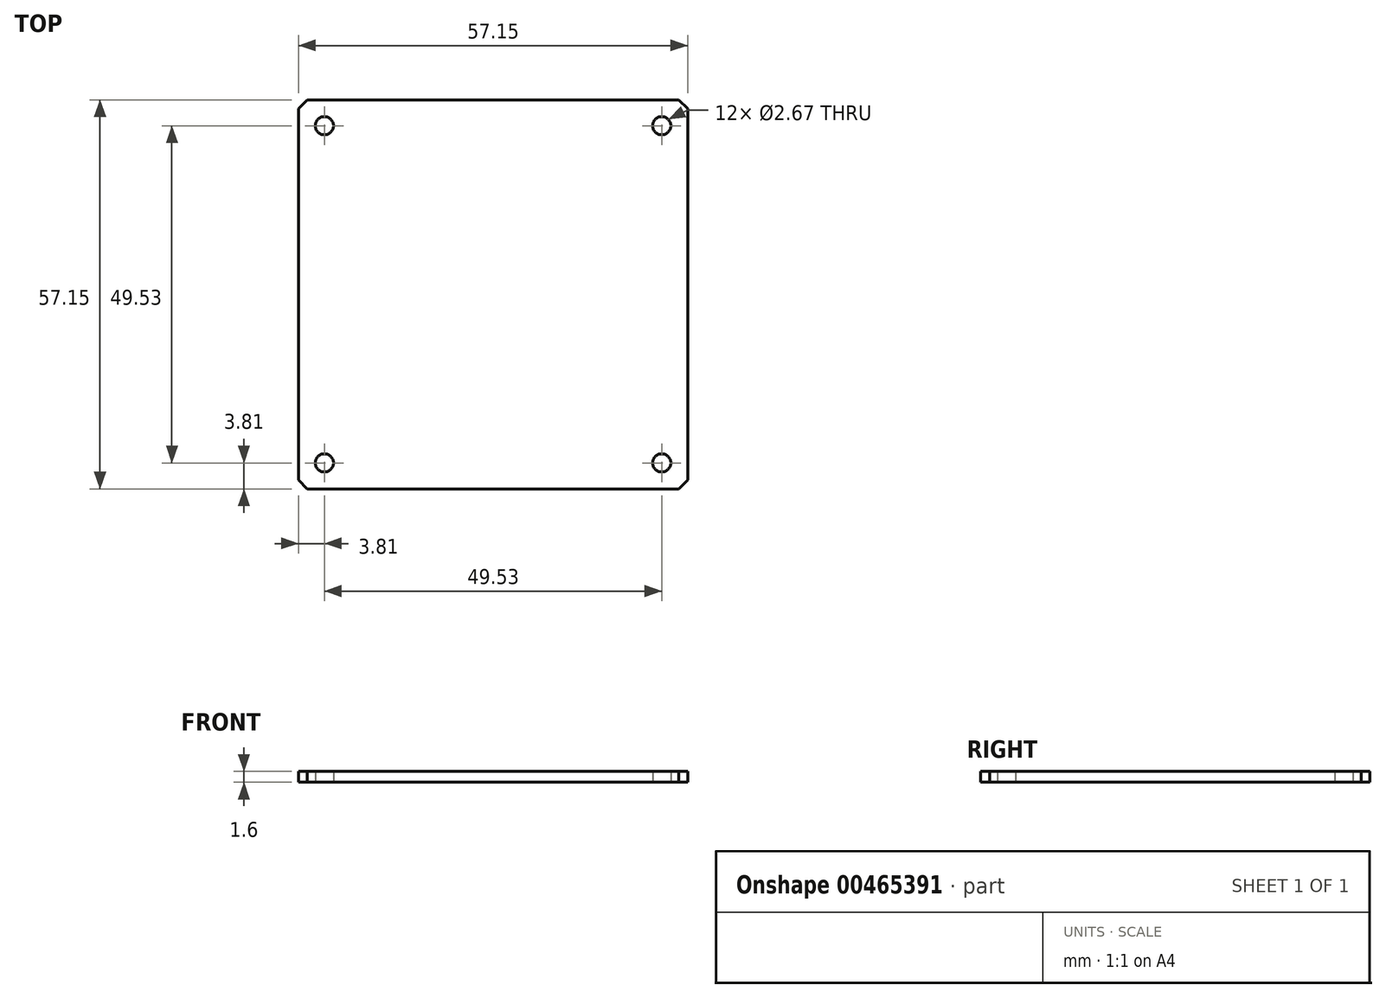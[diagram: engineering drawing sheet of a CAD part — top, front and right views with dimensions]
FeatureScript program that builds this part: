
annotation { "Feature Type Name" : "Feature", "Feature Type Description" : "" }
export const myFeature = defineFeature(function(context is Context, id is Id, definition is map)
    precondition{}
    {
        {
            var Q0;
            Q0=qCreatedBy(makeId("Top.planeOp"),FACE);
            var sketch = newSketch(context, id + "F0", { "sketchPlane" : qUnion([Q0])});
            skLineSegment(sketch, "E0.bottom", {"start": v(0, 0) * mm, "end": v(57.15, 0) * mm});
            skLineSegment(sketch, "E0.top", {"start": v(0, -57.15) * mm, "end": v(57.15, -57.15) * mm});
            skLineSegment(sketch, "E0.left", {"start": v(0, 0) * mm, "end": v(0, -57.15) * mm});
            skLineSegment(sketch, "E0.right", {"start": v(57.15, 0) * mm, "end": v(57.15, -57.15) * mm});
            skCircle(sketch, "E1", {"center": v(53.34, -3.8) * mm, "radius": 1.33 * mm});
            skLineSegment(sketch, "E2", {"start": v(57.15, -28.58) * mm, "end": v(0, -28.58) * mm, "construction": true});
            skLineSegment(sketch, "E3", {"start": v(28.58, 0) * mm, "end": v(28.58, -57.15) * mm, "construction": true});
            skLineSegment(sketch, "E4", {"start": v(55.87, 0) * mm, "end": v(57.15, -1.28) * mm});
            skCircle(sketch, "E5.MirrorC", {"center": v(53.34, -53.34) * mm, "radius": 1.33 * mm});
            skLineSegment(sketch, "E6.MirrorCS", {"start": v(55.87, -57.15) * mm, "end": v(57.15, -55.87) * mm});
            skCircle(sketch, "E7.MirrorC", {"center": v(3.81, -53.34) * mm, "radius": 1.33 * mm});
            skCircle(sketch, "E8.MirrorC", {"center": v(3.81, -3.8) * mm, "radius": 1.33 * mm});
            skLineSegment(sketch, "E9.MirrorCS", {"start": v(1.28, -57.15) * mm, "end": v(0, -55.87) * mm});
            skLineSegment(sketch, "E10.MirrorCS", {"start": v(1.28, 0) * mm, "end": v(0, -1.28) * mm});
            skSolve(sketch);
        }
        {
            var Q0;
            Q0=makeQuery(id+"F0.imprint","IMPRINT",FACE,{"disambiguationData":[TD([[makeQuery(id+"F0.imprint","IMPRINT",EDGE,{"derivedFrom":sQuery(id+"F0.wireOp",EDGE,"E1")}),-1.0]])]});
            extrude(context, id + "F1", {"entities" : qUnion([Q0]), "depth" : 1.6 * mm, "offsetDistance" : 25 * mm});
        }
        {
            var Q0;
            Q0=makeQuery(id+"F1.opExtrude","CAP_FACE",FACE,{"disambiguationData":[OSD([sQuery(id+"F0.wireOp",EDGE,"E0.bottom"),sQuery(id+"F0.wireOp",EDGE,"E0.top"),sQuery(id+"F0.wireOp",EDGE,"E0.left"),sQuery(id+"F0.wireOp",EDGE,"E0.right"),sQuery(id+"F0.wireOp",EDGE,"E1"),sQuery(id+"F0.wireOp",EDGE,"E4"),sQuery(id+"F0.wireOp",EDGE,"E5.MirrorC"),sQuery(id+"F0.wireOp",EDGE,"E6.MirrorCS"),sQuery(id+"F0.wireOp",EDGE,"E7.MirrorC"),sQuery(id+"F0.wireOp",EDGE,"E8.MirrorC"),sQuery(id+"F0.wireOp",EDGE,"E9.MirrorCS"),sQuery(id+"F0.wireOp",EDGE,"E10.MirrorCS")])],"isStart":false});
            var sketch = newSketch(context, id + "F2", { "sketchPlane" : qUnion([Q0])});
            skLineSegment(sketch, "E11", {"start": v(28.58, -57.15) * mm, "end": v(28.58, 0) * mm, "construction": true});
            skPoint(sketch, "E12", {"position": v(28.58, -50.8) * mm});
            skPoint(sketch, "E13", {"position": v(28.58, -6.35) * mm});
            skSolve(sketch);
        }
        {
            var Q0;
            Q0=makeQuery(id+"F1.opExtrude","CAP_FACE",FACE,{"disambiguationData":[OSD([sQuery(id+"F0.wireOp",EDGE,"E0.bottom"),sQuery(id+"F0.wireOp",EDGE,"E0.top"),sQuery(id+"F0.wireOp",EDGE,"E0.left"),sQuery(id+"F0.wireOp",EDGE,"E0.right"),sQuery(id+"F0.wireOp",EDGE,"E1"),sQuery(id+"F0.wireOp",EDGE,"E4"),sQuery(id+"F0.wireOp",EDGE,"E5.MirrorC"),sQuery(id+"F0.wireOp",EDGE,"E6.MirrorCS"),sQuery(id+"F0.wireOp",EDGE,"E7.MirrorC"),sQuery(id+"F0.wireOp",EDGE,"E8.MirrorC"),sQuery(id+"F0.wireOp",EDGE,"E9.MirrorCS"),sQuery(id+"F0.wireOp",EDGE,"E10.MirrorCS")])],"isStart":true});
            var sketch = newSketch(context, id + "F3", { "sketchPlane" : qUnion([Q0])});
            skLineSegment(sketch, "E14", {"start": v(0, 28.58) * mm, "end": v(57.15, 28.58) * mm, "construction": true});
            skPoint(sketch, "E15", {"position": v(6.35, 28.58) * mm});
            skPoint(sketch, "E16", {"position": v(50.8, 28.58) * mm});
            skSolve(sketch);
        }
    });
